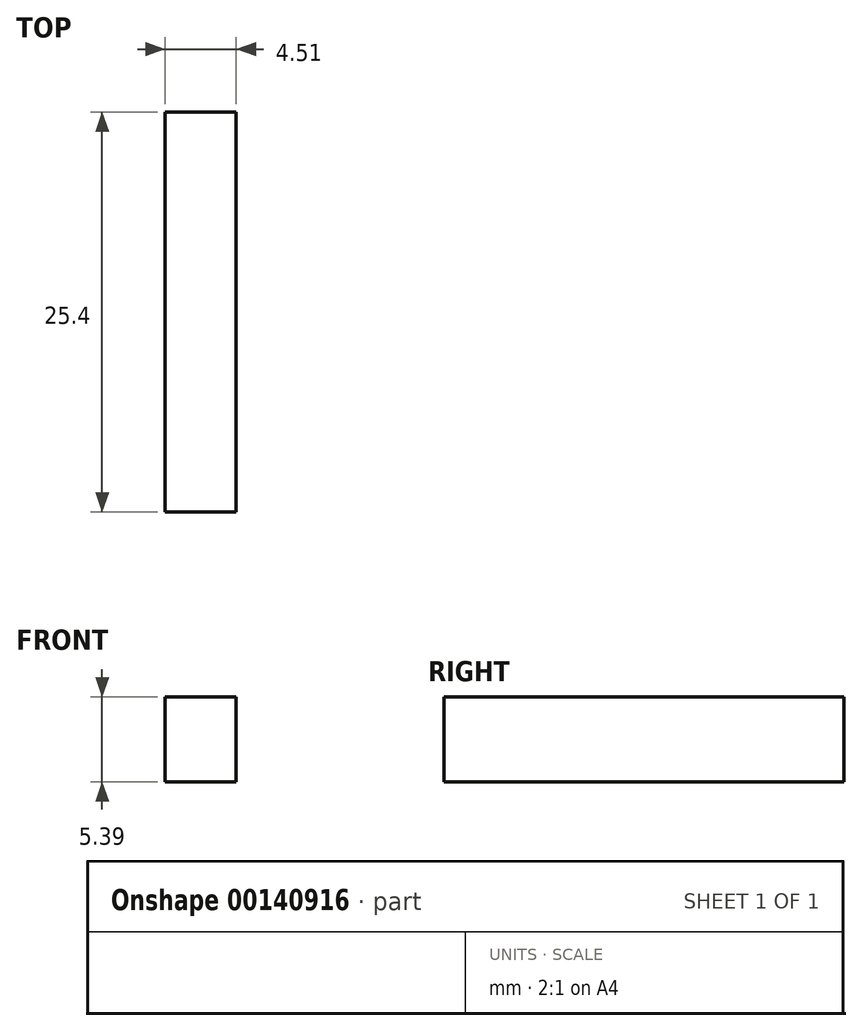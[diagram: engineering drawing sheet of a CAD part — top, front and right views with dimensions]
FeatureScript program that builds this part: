
annotation { "Feature Type Name" : "Feature", "Feature Type Description" : "" }
export const myFeature = defineFeature(function(context is Context, id is Id, definition is map)
    precondition{}
    {
        {
            var Q0;
            Q0=qCreatedBy(makeId("Front.planeOp"),FACE);
            var sketch = newSketch(context, id + "F0", { "sketchPlane" : qUnion([Q0])});
            skLineSegment(sketch, "E0.bottom", {"start": v(-57.94, 66.85) * mm, "end": v(-53.43, 66.85) * mm});
            skLineSegment(sketch, "E0.top", {"start": v(-57.94, 61.46) * mm, "end": v(-53.43, 61.46) * mm});
            skLineSegment(sketch, "E0.left", {"start": v(-57.94, 66.85) * mm, "end": v(-57.94, 61.46) * mm});
            skLineSegment(sketch, "E0.right", {"start": v(-53.43, 66.85) * mm, "end": v(-53.43, 61.46) * mm});
            skSolve(sketch);
        }
        {
            var Q0;
            Q0=sQuery(id+"F0.wireOp",EDGE,"E0.right");
            var Q1;
            Q1=sQuery(id+"F0.wireOp",EDGE,"E0.bottom");
            var Q2;
            Q2=sQuery(id+"F0.wireOp",EDGE,"E0.left");
            var Q3;
            Q3=sQuery(id+"F0.wireOp",EDGE,"E0.top");
            extrude(context, id + "F1", {"bodyType" : ToolBodyType.SURFACE, "surfaceEntities" : qUnion([Q0, Q1, Q2, Q3]), "depth" : 25.4 * mm});
        }
    });
